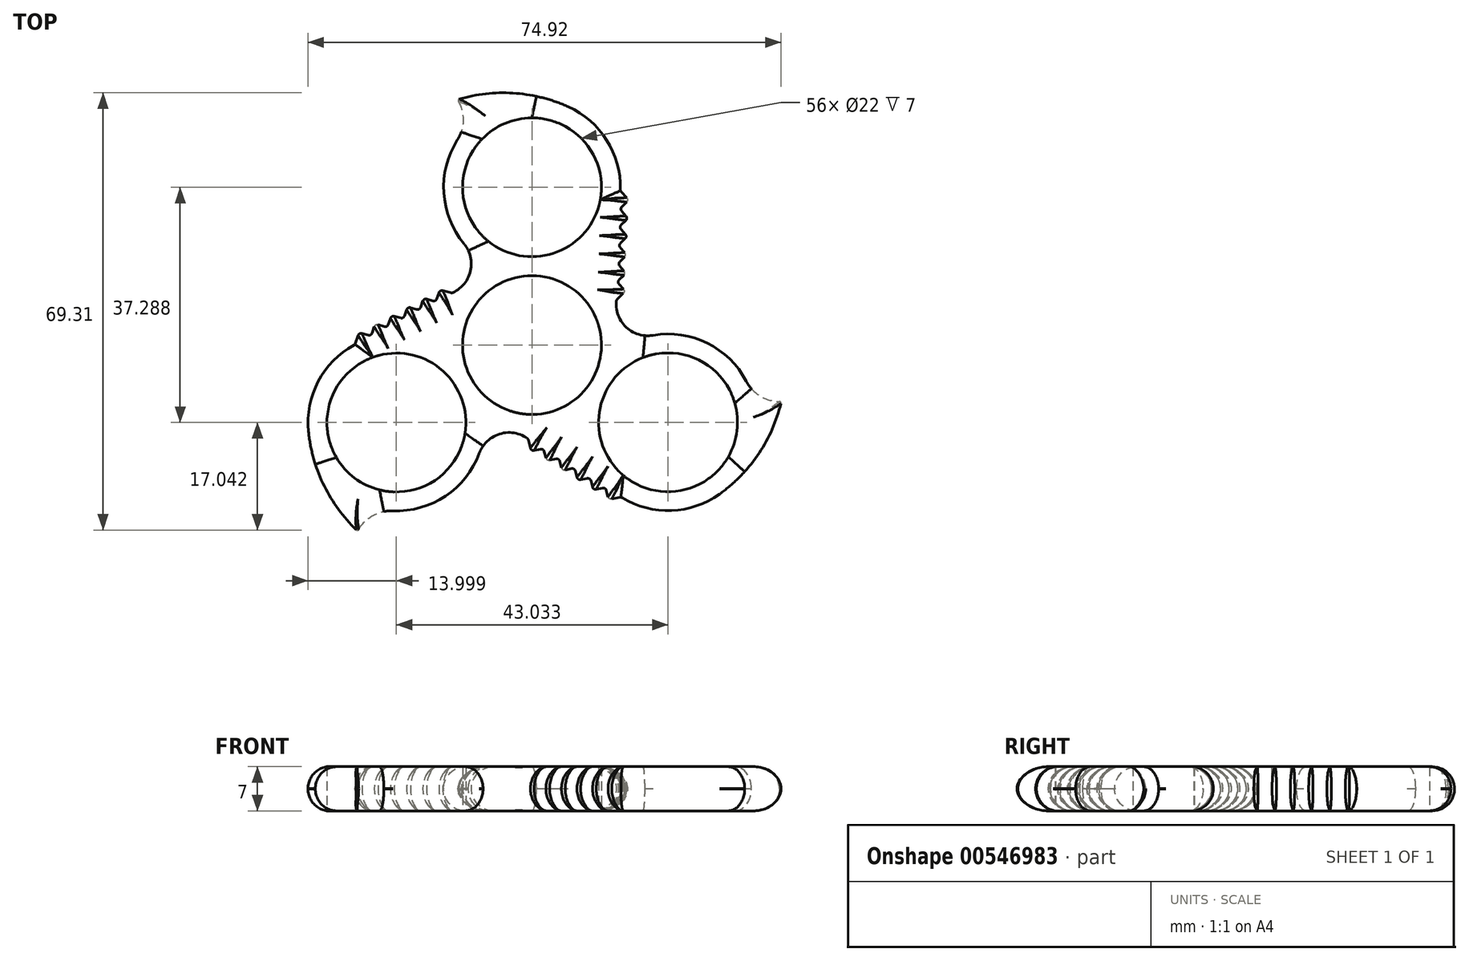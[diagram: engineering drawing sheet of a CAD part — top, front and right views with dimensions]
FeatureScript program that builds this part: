
annotation { "Feature Type Name" : "Feature", "Feature Type Description" : "" }
export const myFeature = defineFeature(function(context is Context, id is Id, definition is map)
    precondition{}
    {
        {
            var Q0;
            Q0=qCreatedBy(makeId("Top.planeOp"),FACE);
            var sketch = newSketch(context, id + "F0", { "sketchPlane" : qUnion([Q0])});
            skCircle(sketch, "E0", {"center": v(0, 0) * mm, "radius": 39 * mm, "construction": true});
            skCircle(sketch, "E1", {"center": v(0, 0) * mm, "radius": 25 * mm, "construction": true});
            skCircle(sketch, "E2", {"center": v(0, 0) * mm, "radius": 11 * mm});
            skCircle(sketch, "E3", {"center": v(0, 25) * mm, "radius": 11 * mm});
            skPoint(sketch, "E4.center", {"position": v(0.03, 0) * mm});
            skArc(sketch, "E5", {"start": v(14, 24.5) * mm, "mid": v(11.9, 32.39) * mm, "end": v(5.75, 37.77) * mm});
            skLineSegment(sketch, "E6", {"start": v(13.35, 6.66) * mm, "end": v(13.36, 7.1) * mm});
            skPoint(sketch, "E7.visualSharp", {"position": v(-4.7, 11.81) * mm});
            skArc(sketch, "E7.filletArc", {"start": v(-12.27, 8.44) * mm, "mid": v(-9.7, 11.89) * mm, "end": v(-10.77, 16.05) * mm});
            skPoint(sketch, "E8.visualSharp", {"position": v(13.05, -1.63) * mm});
            skArc(sketch, "E9", {"start": v(5.75, 37.77) * mm, "mid": v(-2.94, 39.93) * mm, "end": v(-11.83, 38.9) * mm});
            skArc(sketch, "E10", {"start": v(-11.83, 32.48) * mm, "mid": v(-10.9, 35.7) * mm, "end": v(-11.83, 38.9) * mm});
            skArc(sketch, "E11.trimOffspring", {"start": v(-11.83, 32.48) * mm, "mid": v(-13.97, 24.1) * mm, "end": v(-10.77, 16.05) * mm});
            skLineSegment(sketch, "E12", {"start": v(14, 24.5) * mm, "end": v(15.31, 23) * mm});
            skLineSegment(sketch, "E13", {"start": v(15.31, 23) * mm, "end": v(13.89, 21.6) * mm});
            skLineSegment(sketch, "E14.1.0.0", {"start": v(15.2, 20.1) * mm, "end": v(13.78, 18.7) * mm});
            skLineSegment(sketch, "E14.1.0.1", {"start": v(13.89, 21.6) * mm, "end": v(15.2, 20.1) * mm});
            skLineSegment(sketch, "E14.2.0.0", {"start": v(15.1, 17.2) * mm, "end": v(13.68, 15.8) * mm});
            skLineSegment(sketch, "E14.2.0.1", {"start": v(13.78, 18.7) * mm, "end": v(15.1, 17.2) * mm});
            skLineSegment(sketch, "E14.3.0.0", {"start": v(15, 14.3) * mm, "end": v(13.57, 12.9) * mm});
            skLineSegment(sketch, "E14.3.0.1", {"start": v(13.68, 15.8) * mm, "end": v(15, 14.3) * mm});
            skLineSegment(sketch, "E14.4.0.0", {"start": v(14.9, 11.4) * mm, "end": v(13.47, 10) * mm});
            skLineSegment(sketch, "E14.4.0.1", {"start": v(13.57, 12.9) * mm, "end": v(14.9, 11.4) * mm});
            skLineSegment(sketch, "E14.5.0.0", {"start": v(14.79, 8.5) * mm, "end": v(13.36, 7.1) * mm});
            skLineSegment(sketch, "E14.5.0.1", {"start": v(13.47, 10) * mm, "end": v(14.79, 8.5) * mm});
            skArc(sketch, "E15.1.0", {"start": v(-22.04, -26.28) * mm, "mid": v(-25.29, -27.08) * mm, "end": v(-27.6, -29.49) * mm});
            skArc(sketch, "E15.1.1", {"start": v(-1, -14.64) * mm, "mid": v(-5.27, -14.14) * mm, "end": v(-8.35, -17.14) * mm});
            skArc(sketch, "E15.1.2", {"start": v(-22.04, -26.28) * mm, "mid": v(-13.71, -23.93) * mm, "end": v(-8.35, -17.14) * mm});
            skArc(sketch, "E15.1.3", {"start": v(-35.41, -13.7) * mm, "mid": v(-32.94, -22.3) * mm, "end": v(-27.6, -29.49) * mm});
            skArc(sketch, "E15.1.4", {"start": v(-28.04, 0.08) * mm, "mid": v(-33.82, -5.68) * mm, "end": v(-35.41, -13.7) * mm});
            skCircle(sketch, "E15.1.5", {"center": v(-21.48, -12.29) * mm, "radius": 11 * mm});
            skLineSegment(sketch, "E15.1.6", {"start": v(-28.04, 0.08) * mm, "end": v(-27.4, 1.98) * mm});
            skLineSegment(sketch, "E15.1.7", {"start": v(-27.4, 1.98) * mm, "end": v(-25.47, 1.44) * mm});
            skLineSegment(sketch, "E15.1.8", {"start": v(-25.48, 1.44) * mm, "end": v(-24.84, 3.34) * mm});
            skLineSegment(sketch, "E15.1.9", {"start": v(-24.84, 3.34) * mm, "end": v(-22.91, 2.8) * mm});
            skLineSegment(sketch, "E15.1.10", {"start": v(-22.91, 2.8) * mm, "end": v(-22.28, 4.7) * mm});
            skLineSegment(sketch, "E15.1.11", {"start": v(-22.28, 4.7) * mm, "end": v(-20.35, 4.16) * mm});
            skLineSegment(sketch, "E15.1.12", {"start": v(-20.35, 4.16) * mm, "end": v(-19.71, 6.05) * mm});
            skLineSegment(sketch, "E15.1.13", {"start": v(-19.71, 6.05) * mm, "end": v(-17.79, 5.52) * mm});
            skLineSegment(sketch, "E15.1.14", {"start": v(-17.79, 5.51) * mm, "end": v(-17.15, 7.41) * mm});
            skLineSegment(sketch, "E15.1.15", {"start": v(-17.15, 7.41) * mm, "end": v(-15.23, 6.87) * mm});
            skLineSegment(sketch, "E15.1.16", {"start": v(-15.23, 6.87) * mm, "end": v(-14.59, 8.77) * mm});
            skLineSegment(sketch, "E15.1.17", {"start": v(-14.59, 8.77) * mm, "end": v(-12.66, 8.23) * mm});
            skLineSegment(sketch, "E15.1.18", {"start": v(-12.27, 8.44) * mm, "end": v(-12.66, 8.23) * mm});
            skArc(sketch, "E15.2.0", {"start": v(33.95, -5.74) * mm, "mid": v(36.26, -8.15) * mm, "end": v(39.5, -8.95) * mm});
            skArc(sketch, "E15.2.1", {"start": v(13.35, 6.66) * mm, "mid": v(15.05, 2.72) * mm, "end": v(19.19, 1.55) * mm});
            skArc(sketch, "E15.2.2", {"start": v(33.95, -5.74) * mm, "mid": v(27.75, 0.3) * mm, "end": v(19.19, 1.55) * mm});
            skArc(sketch, "E15.2.3", {"start": v(29.73, -23.6) * mm, "mid": v(35.95, -17.16) * mm, "end": v(39.5, -8.95) * mm});
            skArc(sketch, "E15.2.4", {"start": v(14.12, -24.11) * mm, "mid": v(22, -26.24) * mm, "end": v(29.73, -23.6) * mm});
            skCircle(sketch, "E15.2.5", {"center": v(21.55, -12.25) * mm, "radius": 11 * mm});
            skLineSegment(sketch, "E15.2.6", {"start": v(14.12, -24.11) * mm, "end": v(12.16, -24.5) * mm});
            skLineSegment(sketch, "E15.2.7", {"start": v(12.16, -24.5) * mm, "end": v(11.66, -22.57) * mm});
            skLineSegment(sketch, "E15.2.8", {"start": v(11.66, -22.57) * mm, "end": v(9.7, -22.97) * mm});
            skLineSegment(sketch, "E15.2.9", {"start": v(9.7, -22.97) * mm, "end": v(9.2, -21.03) * mm});
            skLineSegment(sketch, "E15.2.10", {"start": v(9.2, -21.03) * mm, "end": v(7.24, -21.43) * mm});
            skLineSegment(sketch, "E15.2.11", {"start": v(7.24, -21.43) * mm, "end": v(6.74, -19.5) * mm});
            skLineSegment(sketch, "E15.2.12", {"start": v(6.75, -19.5) * mm, "end": v(4.79, -19.89) * mm});
            skLineSegment(sketch, "E15.2.13", {"start": v(4.79, -19.89) * mm, "end": v(4.29, -17.95) * mm});
            skLineSegment(sketch, "E15.2.14", {"start": v(4.29, -17.95) * mm, "end": v(2.33, -18.35) * mm});
            skLineSegment(sketch, "E15.2.15", {"start": v(2.33, -18.35) * mm, "end": v(1.83, -16.41) * mm});
            skLineSegment(sketch, "E15.2.16", {"start": v(1.83, -16.41) * mm, "end": v(-0.13, -16.8) * mm});
            skLineSegment(sketch, "E15.2.17", {"start": v(-0.13, -16.8) * mm, "end": v(-0.63, -14.87) * mm});
            skLineSegment(sketch, "E15.2.18", {"start": v(-1, -14.64) * mm, "end": v(-0.63, -14.87) * mm});
            skPoint(sketch, "E15.center", {"position": v(0.02, 0.15) * mm});
            skLineSegment(sketch, "E16.trimOffspring", {"start": v(-25.47, 1.44) * mm, "end": v(-25.48, 1.44) * mm});
            skLineSegment(sketch, "E17.trimOffspring", {"start": v(-22.91, 2.8) * mm, "end": v(-22.91, 2.8) * mm});
            skLineSegment(sketch, "E18.trimOffspring", {"start": v(-20.35, 4.16) * mm, "end": v(-20.35, 4.16) * mm});
            skLineSegment(sketch, "E19.trimOffspring", {"start": v(-17.79, 5.52) * mm, "end": v(-17.79, 5.51) * mm});
            skLineSegment(sketch, "E20.trimOffspring", {"start": v(-15.23, 6.87) * mm, "end": v(-15.23, 6.87) * mm});
            skLineSegment(sketch, "E21.trimOffspring", {"start": v(1.83, -16.41) * mm, "end": v(1.83, -16.41) * mm});
            skLineSegment(sketch, "E22.trimOffspring", {"start": v(4.29, -17.95) * mm, "end": v(4.29, -17.95) * mm});
            skLineSegment(sketch, "E23.trimOffspring", {"start": v(6.74, -19.5) * mm, "end": v(6.75, -19.5) * mm});
            skLineSegment(sketch, "E24.trimOffspring", {"start": v(9.2, -21.03) * mm, "end": v(9.2, -21.03) * mm});
            skLineSegment(sketch, "E25.trimOffspring", {"start": v(11.26, -22.32) * mm, "end": v(11.66, -22.57) * mm});
            skLineSegment(sketch, "E26.trimOffspring", {"start": v(13.47, 10) * mm, "end": v(13.47, 10) * mm});
            skLineSegment(sketch, "E27.trimOffspring", {"start": v(13.57, 12.9) * mm, "end": v(13.57, 12.9) * mm});
            skLineSegment(sketch, "E28.trimOffspring", {"start": v(13.68, 15.8) * mm, "end": v(13.68, 15.8) * mm});
            skLineSegment(sketch, "E29.trimOffspring", {"start": v(13.78, 18.7) * mm, "end": v(13.78, 18.7) * mm});
            skLineSegment(sketch, "E30.trimOffspring", {"start": v(13.78, 18.7) * mm, "end": v(13.78, 18.7) * mm, "construction": true});
            skLineSegment(sketch, "E31.trimOffspring", {"start": v(13.89, 21.6) * mm, "end": v(13.89, 21.6) * mm});
            skSolve(sketch);
        }
        {
            var Q0;
            Q0 = qSketchRegion(id + "F0", true);
            extrude(context, id + "F1", {"entities" : qUnion([Q0]), "depth" : 7 * mm, "offsetDistance" : 25 * mm});
        }
        {
            var Q0;
            Q0=makeQuery(id+"F1.opExtrude","SWEPT_EDGE",EDGE,{"disambiguationData":[OSD([sQuery(id+"F0.wireOp",EDGE,"E15.1.17"),sQuery(id+"F0.wireOp",EDGE,"E15.1.18")])]});
            var Q1;
            Q1=makeQuery(id+"F1.opExtrude","SWEPT_EDGE",EDGE,{"disambiguationData":[OSD([sQuery(id+"F0.wireOp",EDGE,"E15.1.16"),sQuery(id+"F0.wireOp",EDGE,"E15.1.17")])]});
            var Q2;
            Q2=makeQuery(id+"F1.opExtrude","SWEPT_EDGE",EDGE,{"disambiguationData":[OSD([sQuery(id+"F0.wireOp",EDGE,"E15.1.15"),sQuery(id+"F0.wireOp",EDGE,"E15.1.16")])]});
            var Q3;
            Q3=makeQuery(id+"F1.opExtrude","SWEPT_EDGE",EDGE,{"disambiguationData":[OSD([sQuery(id+"F0.wireOp",EDGE,"E15.1.14"),sQuery(id+"F0.wireOp",EDGE,"E15.1.15")])]});
            var Q4;
            Q4=makeQuery(id+"F1.opExtrude","SWEPT_EDGE",EDGE,{"disambiguationData":[OSD([sQuery(id+"F0.wireOp",EDGE,"E15.1.13"),sQuery(id+"F0.wireOp",EDGE,"E15.1.14")])]});
            var Q5;
            Q5=makeQuery(id+"F1.opExtrude","SWEPT_EDGE",EDGE,{"disambiguationData":[OSD([sQuery(id+"F0.wireOp",EDGE,"E15.1.12"),sQuery(id+"F0.wireOp",EDGE,"E15.1.13")])]});
            var Q6;
            Q6=makeQuery(id+"F1.opExtrude","SWEPT_EDGE",EDGE,{"disambiguationData":[OSD([sQuery(id+"F0.wireOp",EDGE,"E15.1.11"),sQuery(id+"F0.wireOp",EDGE,"E15.1.12")])]});
            var Q7;
            Q7=makeQuery(id+"F1.opExtrude","SWEPT_EDGE",EDGE,{"disambiguationData":[OSD([sQuery(id+"F0.wireOp",EDGE,"E15.1.10"),sQuery(id+"F0.wireOp",EDGE,"E15.1.11")])]});
            var Q8;
            Q8=makeQuery(id+"F1.opExtrude","SWEPT_EDGE",EDGE,{"disambiguationData":[OSD([sQuery(id+"F0.wireOp",EDGE,"E15.1.9"),sQuery(id+"F0.wireOp",EDGE,"E15.1.10")])]});
            var Q9;
            Q9=makeQuery(id+"F1.opExtrude","SWEPT_EDGE",EDGE,{"disambiguationData":[OSD([sQuery(id+"F0.wireOp",EDGE,"E15.1.8"),sQuery(id+"F0.wireOp",EDGE,"E15.1.9")])]});
            var Q10;
            Q10=makeQuery(id+"F1.opExtrude","SWEPT_EDGE",EDGE,{"disambiguationData":[OSD([sQuery(id+"F0.wireOp",EDGE,"E15.1.7"),sQuery(id+"F0.wireOp",EDGE,"E15.1.8")])]});
            var Q11;
            Q11=makeQuery(id+"F1.opExtrude","SWEPT_EDGE",EDGE,{"disambiguationData":[OSD([sQuery(id+"F0.wireOp",EDGE,"E15.1.6"),sQuery(id+"F0.wireOp",EDGE,"E15.1.7")])]});
            var Q12;
            Q12=makeQuery(id+"F1.opExtrude","SWEPT_EDGE",EDGE,{"disambiguationData":[OSD([sQuery(id+"F0.wireOp",EDGE,"E15.1.4"),sQuery(id+"F0.wireOp",EDGE,"E15.1.6")])]});
            var Q13;
            Q13=makeQuery(id+"F1.opExtrude","SWEPT_EDGE",EDGE,{"disambiguationData":[OSD([sQuery(id+"F0.wireOp",EDGE,"E15.2.17"),sQuery(id+"F0.wireOp",EDGE,"E15.2.18")])]});
            var Q14;
            Q14=makeQuery(id+"F1.opExtrude","SWEPT_EDGE",EDGE,{"disambiguationData":[OSD([sQuery(id+"F0.wireOp",EDGE,"E15.2.16"),sQuery(id+"F0.wireOp",EDGE,"E15.2.17")])]});
            var Q15;
            Q15=makeQuery(id+"F1.opExtrude","SWEPT_EDGE",EDGE,{"disambiguationData":[OSD([sQuery(id+"F0.wireOp",EDGE,"E15.2.15"),sQuery(id+"F0.wireOp",EDGE,"E15.2.16")])]});
            var Q16;
            Q16=makeQuery(id+"F1.opExtrude","SWEPT_EDGE",EDGE,{"disambiguationData":[OSD([sQuery(id+"F0.wireOp",EDGE,"E15.2.14"),sQuery(id+"F0.wireOp",EDGE,"E15.2.15")])]});
            var Q17;
            Q17=makeQuery(id+"F1.opExtrude","SWEPT_EDGE",EDGE,{"disambiguationData":[OSD([sQuery(id+"F0.wireOp",EDGE,"E15.2.13"),sQuery(id+"F0.wireOp",EDGE,"E15.2.14")])]});
            var Q18;
            Q18=makeQuery(id+"F1.opExtrude","SWEPT_EDGE",EDGE,{"disambiguationData":[OSD([sQuery(id+"F0.wireOp",EDGE,"E15.2.12"),sQuery(id+"F0.wireOp",EDGE,"E15.2.13")])]});
            var Q19;
            Q19=makeQuery(id+"F1.opExtrude","SWEPT_EDGE",EDGE,{"disambiguationData":[OSD([sQuery(id+"F0.wireOp",EDGE,"E15.2.11"),sQuery(id+"F0.wireOp",EDGE,"E15.2.12")])]});
            var Q20;
            Q20=makeQuery(id+"F1.opExtrude","SWEPT_EDGE",EDGE,{"disambiguationData":[OSD([sQuery(id+"F0.wireOp",EDGE,"E15.2.10"),sQuery(id+"F0.wireOp",EDGE,"E15.2.11")])]});
            var Q21;
            Q21=makeQuery(id+"F1.opExtrude","SWEPT_EDGE",EDGE,{"disambiguationData":[OSD([sQuery(id+"F0.wireOp",EDGE,"E15.2.9"),sQuery(id+"F0.wireOp",EDGE,"E15.2.10")])]});
            var Q22;
            Q22=makeQuery(id+"F1.opExtrude","SWEPT_EDGE",EDGE,{"disambiguationData":[OSD([sQuery(id+"F0.wireOp",EDGE,"E15.2.8"),sQuery(id+"F0.wireOp",EDGE,"E15.2.9")])]});
            var Q23;
            Q23=makeQuery(id+"F1.opExtrude","SWEPT_EDGE",EDGE,{"disambiguationData":[OSD([sQuery(id+"F0.wireOp",EDGE,"E15.2.7"),sQuery(id+"F0.wireOp",EDGE,"E15.2.8")])]});
            var Q24;
            Q24=makeQuery(id+"F1.opExtrude","SWEPT_EDGE",EDGE,{"disambiguationData":[OSD([sQuery(id+"F0.wireOp",EDGE,"E15.2.6"),sQuery(id+"F0.wireOp",EDGE,"E15.2.7")])]});
            var Q25;
            Q25=makeQuery(id+"F1.opExtrude","SWEPT_EDGE",EDGE,{"disambiguationData":[OSD([sQuery(id+"F0.wireOp",EDGE,"E15.2.4"),sQuery(id+"F0.wireOp",EDGE,"E15.2.6")])]});
            var Q26;
            Q26=makeQuery(id+"F1.opExtrude","SWEPT_EDGE",EDGE,{"disambiguationData":[OSD([sQuery(id+"F0.wireOp",EDGE,"E5"),sQuery(id+"F0.wireOp",EDGE,"E12")])]});
            var Q27;
            Q27=makeQuery(id+"F1.opExtrude","SWEPT_EDGE",EDGE,{"disambiguationData":[OSD([sQuery(id+"F0.wireOp",EDGE,"E12"),sQuery(id+"F0.wireOp",EDGE,"E13")])]});
            var Q28;
            Q28=makeQuery(id+"F1.opExtrude","SWEPT_EDGE",EDGE,{"disambiguationData":[OSD([sQuery(id+"F0.wireOp",EDGE,"E13"),sQuery(id+"F0.wireOp",EDGE,"E14.1.0.1")])]});
            var Q29;
            Q29=makeQuery(id+"F1.opExtrude","SWEPT_EDGE",EDGE,{"disambiguationData":[OSD([sQuery(id+"F0.wireOp",EDGE,"E14.1.0.0"),sQuery(id+"F0.wireOp",EDGE,"E14.1.0.1")])]});
            var Q30;
            Q30=makeQuery(id+"F1.opExtrude","SWEPT_EDGE",EDGE,{"disambiguationData":[OSD([sQuery(id+"F0.wireOp",EDGE,"E14.1.0.0"),sQuery(id+"F0.wireOp",EDGE,"E14.2.0.1")])]});
            var Q31;
            Q31=makeQuery(id+"F1.opExtrude","SWEPT_EDGE",EDGE,{"disambiguationData":[OSD([sQuery(id+"F0.wireOp",EDGE,"E14.2.0.0"),sQuery(id+"F0.wireOp",EDGE,"E14.2.0.1")])]});
            var Q32;
            Q32=makeQuery(id+"F1.opExtrude","SWEPT_EDGE",EDGE,{"disambiguationData":[OSD([sQuery(id+"F0.wireOp",EDGE,"E14.2.0.0"),sQuery(id+"F0.wireOp",EDGE,"E14.3.0.1")])]});
            var Q33;
            Q33=makeQuery(id+"F1.opExtrude","SWEPT_EDGE",EDGE,{"disambiguationData":[OSD([sQuery(id+"F0.wireOp",EDGE,"E14.3.0.0"),sQuery(id+"F0.wireOp",EDGE,"E14.3.0.1")])]});
            var Q34;
            Q34=makeQuery(id+"F1.opExtrude","SWEPT_EDGE",EDGE,{"disambiguationData":[OSD([sQuery(id+"F0.wireOp",EDGE,"E14.3.0.0"),sQuery(id+"F0.wireOp",EDGE,"E14.4.0.1")])]});
            var Q35;
            Q35=makeQuery(id+"F1.opExtrude","SWEPT_EDGE",EDGE,{"disambiguationData":[OSD([sQuery(id+"F0.wireOp",EDGE,"E14.4.0.0"),sQuery(id+"F0.wireOp",EDGE,"E14.4.0.1")])]});
            var Q36;
            Q36=makeQuery(id+"F1.opExtrude","SWEPT_EDGE",EDGE,{"disambiguationData":[OSD([sQuery(id+"F0.wireOp",EDGE,"E14.4.0.0"),sQuery(id+"F0.wireOp",EDGE,"E14.5.0.1")])]});
            var Q37;
            Q37=makeQuery(id+"F1.opExtrude","SWEPT_EDGE",EDGE,{"disambiguationData":[OSD([sQuery(id+"F0.wireOp",EDGE,"E14.5.0.0"),sQuery(id+"F0.wireOp",EDGE,"E14.5.0.1")])]});
            var Q38;
            Q38=makeQuery(id+"F1.opExtrude","SWEPT_EDGE",EDGE,{"disambiguationData":[OSD([sQuery(id+"F0.wireOp",EDGE,"E6"),sQuery(id+"F0.wireOp",EDGE,"E14.5.0.0")])]});
            fillet(context, id + "F2", {"entities" : qUnion([Q0, Q1, Q2, Q3, Q4, Q5, Q6, Q7, Q8, Q9, Q10, Q11, Q12, Q13, Q14, Q15, Q16, Q17, Q18, Q19, Q20, Q21, Q22, Q23, Q24, Q25, Q26, Q27, Q28, Q29, Q30, Q31, Q32, Q33, Q34, Q35, Q36, Q37, Q38]), "radius" : .5 * mm, "tangentPropagation" : true, "allowEdgeOverflow" : false});
        }
        {
            var Q0;
            Q0=makeQuery(id+"F1.opExtrude","SWEPT_EDGE",EDGE,{"disambiguationData":[OSD([sQuery(id+"F0.wireOp",EDGE,"E9"),sQuery(id+"F0.wireOp",EDGE,"E10")])]});
            var Q1;
            Q1=makeQuery(id+"F1.opExtrude","SWEPT_EDGE",EDGE,{"disambiguationData":[OSD([sQuery(id+"F0.wireOp",EDGE,"E15.1.0"),sQuery(id+"F0.wireOp",EDGE,"E15.1.3")])]});
            var Q2;
            Q2=makeQuery(id+"F1.opExtrude","SWEPT_EDGE",EDGE,{"disambiguationData":[OSD([sQuery(id+"F0.wireOp",EDGE,"E15.2.0"),sQuery(id+"F0.wireOp",EDGE,"E15.2.3")])]});
            fillet(context, id + "F3", {"entities" : qUnion([Q0, Q1, Q2]), "radius" : .25 * mm, "tangentPropagation" : true, "allowEdgeOverflow" : false});
        }
        {
            var Q0;
            Q0=makeQuery(id+"F1.opExtrude","CAP_EDGE",EDGE,{"disambiguationData":[OSD([sQuery(id+"F0.wireOp",EDGE,"E15.2.4")])],"isStart":false});
            var Q1;
            Q1=makeQuery(id+"F1.opExtrude","CAP_EDGE",EDGE,{"disambiguationData":[OSD([sQuery(id+"F0.wireOp",EDGE,"E15.1.1")])],"isStart":true});
            fillet(context, id + "F4", {"entities" : qUnion([Q0, Q1]), "radius" : 3.5 * mm, "tangentPropagation" : true, "allowEdgeOverflow" : false});
        }
    });
